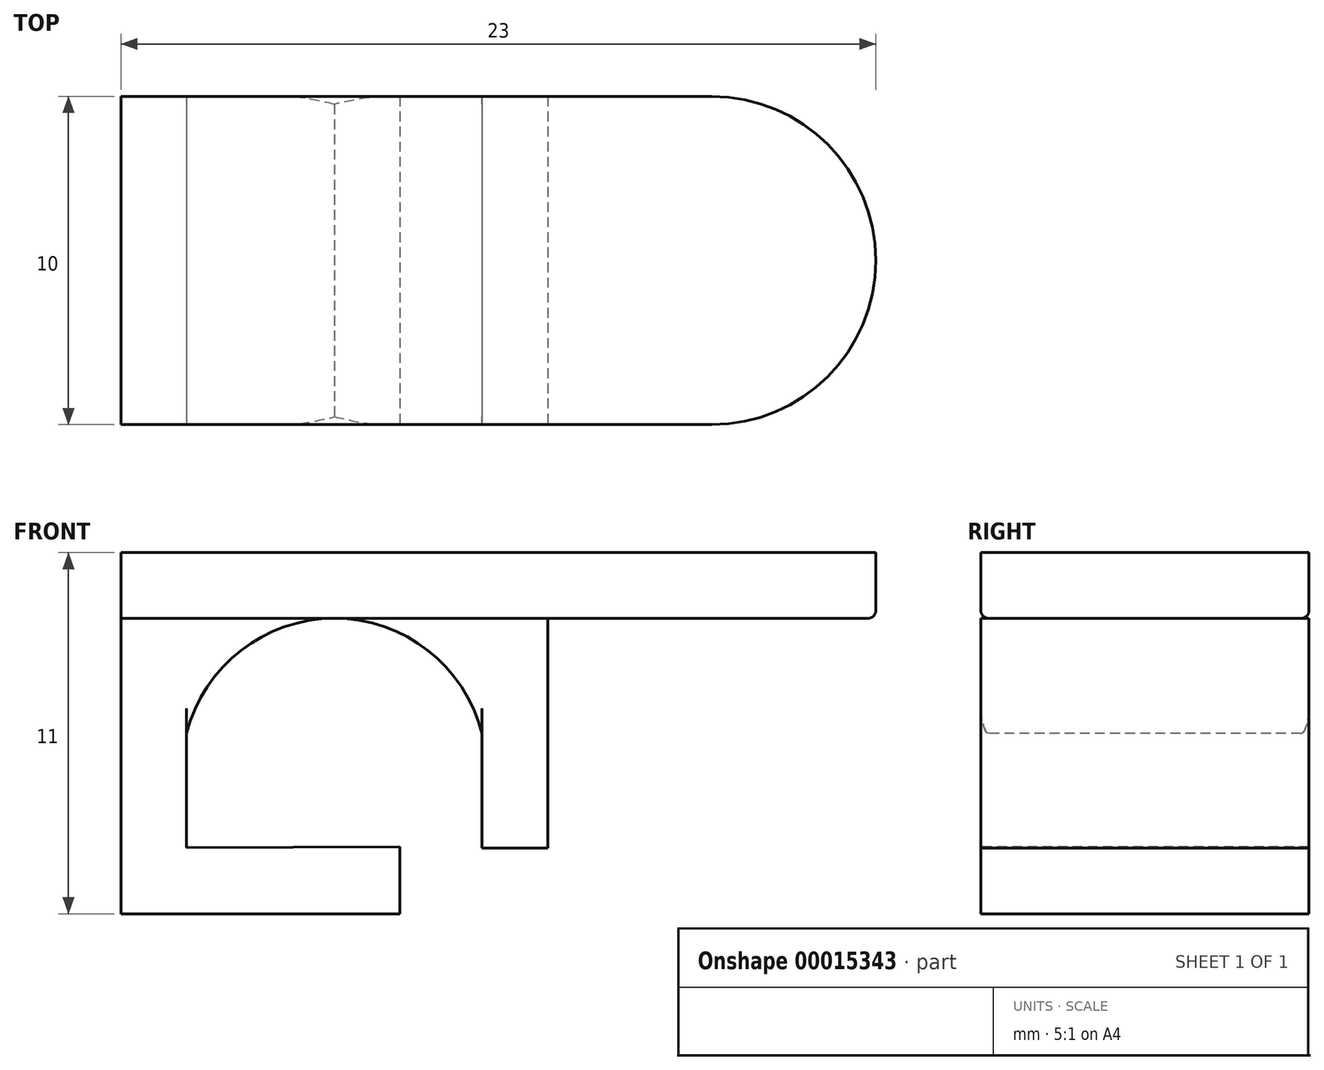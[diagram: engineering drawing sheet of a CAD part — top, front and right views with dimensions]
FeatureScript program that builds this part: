
annotation { "Feature Type Name" : "Feature", "Feature Type Description" : "" }
export const myFeature = defineFeature(function(context is Context, id is Id, definition is map)
    precondition{}
    {
        {
            var Q0;
            Q0=qCreatedBy(makeId("Top.planeOp"),FACE);
            var sketch = newSketch(context, id + "F0", { "sketchPlane" : qUnion([Q0])});
            skLineSegment(sketch, "E0", {"start": v(0, 5) * mm, "end": v(-5, 5) * mm});
            skLineSegment(sketch, "E1", {"start": v(0, -5) * mm, "end": v(-5, -5) * mm});
            skLineSegment(sketch, "E2", {"start": v(-5, -5) * mm, "end": v(-5, 5) * mm, "construction": true});
            skArc(sketch, "E3", {"start": v(0, -5) * mm, "mid": v(5, 0) * mm, "end": v(0, 5) * mm});
            skLineSegment(sketch, "E4", {"start": v(-5, 5) * mm, "end": v(-18, 5) * mm});
            skLineSegment(sketch, "E5", {"start": v(-18, 5) * mm, "end": v(-18, -5) * mm});
            skLineSegment(sketch, "E6", {"start": v(-18, -5) * mm, "end": v(-5, -5) * mm});
            skSolve(sketch);
        }
        {
            var Q0;
            Q0=qSketchRegion(id+"F0",true);
            extrude(context, id + "F1", {"entities" : qUnion([Q0]), "depth" : 2 * mm});
        }
        {
            var Q0;
            Q0=makeQuery(id+"F1.opExtrude","SWEPT_FACE",FACE,{"disambiguationData":[OSD([sQuery(id+"F0.wireOp",EDGE,"E1"),sQuery(id+"F0.wireOp",EDGE,"E6")])]});
            var sketch = newSketch(context, id + "F2", { "sketchPlane" : qUnion([Q0])});
            skLineSegment(sketch, "E7", {"start": v(-18, 0) * mm, "end": v(-18, -7) * mm});
            skLineSegment(sketch, "E8", {"start": v(0, 0) * mm, "end": v(-5, 0) * mm, "construction": true});
            skLineSegment(sketch, "E9", {"start": v(-5, 0) * mm, "end": v(-5, -7) * mm});
            skLineSegment(sketch, "E10", {"start": v(-5, 0) * mm, "end": v(-18, 0) * mm});
            skLineSegment(sketch, "E11", {"start": v(0, 0) * mm, "end": v(0, -3.5) * mm, "construction": true});
            skLineSegment(sketch, "E12", {"start": v(-5, 0) * mm, "end": v(-5, 2.92) * mm, "construction": true});
            skLineSegment(sketch, "E13", {"start": v(-18, -7) * mm, "end": v(-16, -7) * mm});
            skLineSegment(sketch, "E14", {"start": v(-16, -7) * mm, "end": v(-16, 0) * mm});
            skLineSegment(sketch, "E15", {"start": v(-5, -7) * mm, "end": v(-7, -7) * mm});
            skLineSegment(sketch, "E16", {"start": v(-7, -7) * mm, "end": v(-7, 0) * mm});
            skArc(sketch, "E17", {"start": v(-7, -3.5) * mm, "mid": v(-8.65, -0.98) * mm, "end": v(-11.5, 0) * mm});
            skArc(sketch, "E18", {"start": v(-11.5, 0) * mm, "mid": v(-14.35, -0.98) * mm, "end": v(-16, -3.5) * mm});
            skSolve(sketch);
        }
        {
            var Q0;
            Q0=qSketchRegion(id+"F2",true);
            extrude(context, id + "F3", {"entities" : qUnion([Q0]), "oppositeDirection" : true, "depth" : 10 * mm});
        }
        {
            var Q0;
            Q0=makeQuery(id+"F3.opExtrude","CAP_FACE",FACE,{"disambiguationData":[OSD([sQuery(id+"F2.wireOp",EDGE,"E7"),sQuery(id+"F2.wireOp",EDGE,"E10"),sQuery(id+"F2.wireOp",EDGE,"E13"),sQuery(id+"F2.wireOp",EDGE,"E14"),sQuery(id+"F2.wireOp",EDGE,"E18")])],"isStart":true});
            var sketch = newSketch(context, id + "F4", { "sketchPlane" : qUnion([Q0])});
            skLineSegment(sketch, "E19", {"start": v(-18, -7) * mm, "end": v(-18, -9) * mm});
            skLineSegment(sketch, "E20", {"start": v(-18, -9) * mm, "end": v(-9.5, -9) * mm});
            skLineSegment(sketch, "E21", {"start": v(-9.5, -9) * mm, "end": v(-9.5, -6.96) * mm});
            skLineSegment(sketch, "E22", {"start": v(-9.5, -6.96) * mm, "end": v(-18, -7) * mm});
            skSolve(sketch);
        }
        {
            var Q0;
            Q0=qSketchRegion(id+"F4",true);
            extrude(context, id + "F5", {"entities" : qUnion([Q0]), "operationType" : NewBodyOperationType.ADD, "oppositeDirection" : true, "depth" : 10 * mm});
        }
        {
            var Q0;
            Q0=makeQuery(id+"F3.opExtrude","CAP_EDGE",EDGE,{"disambiguationData":[OSD([sQuery(id+"F2.wireOp",EDGE,"E18")])],"isStart":true});
            var Q1;
            Q1=makeQuery(id+"F3.opExtrude","CAP_EDGE",EDGE,{"disambiguationData":[OSD([sQuery(id+"F2.wireOp",EDGE,"E17")])],"isStart":true});
            var Q2;
            Q2=makeQuery(id+"F3.opExtrude","CAP_EDGE",EDGE,{"disambiguationData":[OSD([sQuery(id+"F2.wireOp",EDGE,"E18")])],"isStart":false});
            var Q3;
            Q3=makeQuery(id+"F3.opExtrude","CAP_EDGE",EDGE,{"disambiguationData":[OSD([sQuery(id+"F2.wireOp",EDGE,"E17")])],"isStart":false});
            fillet(context, id + "F6", {"entities" : qUnion([Q0, Q1, Q2, Q3]), "radius" : 0.24 * mm, "tangentPropagation" : true, "allowEdgeOverflow" : false});
        }
        {
            var Q0;
            Q0=makeQuery(id+"F1.opExtrude","CAP_EDGE",EDGE,{"disambiguationData":[OSD([sQuery(id+"F0.wireOp",EDGE,"E1"),sQuery(id+"F0.wireOp",EDGE,"E6")])],"isStart":true});
            var Q1;
            Q1=makeQuery(id+"F1.opExtrude","CAP_EDGE",EDGE,{"disambiguationData":[OSD([sQuery(id+"F0.wireOp",EDGE,"E0"),sQuery(id+"F0.wireOp",EDGE,"E4")])],"isStart":true});
            fillet(context, id + "F7", {"entities" : qUnion([Q0, Q1]), "radius" : 0.24 * mm, "tangentPropagation" : true, "allowEdgeOverflow" : false});
        }
    });
